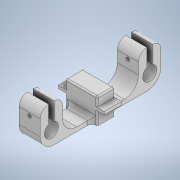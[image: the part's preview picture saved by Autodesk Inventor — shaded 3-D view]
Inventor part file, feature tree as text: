
AUTODESK INVENTOR PART (.ipt)
format: ipt  version: 2022 (Build 260153000, 153)  size: 273,920 bytes
history: native  units: mm
features: extrude x8, sketch x8, fillet x6
ambient origin geometry x8: Origin, YZ Plane, XZ Plane, XY Plane, X Axis, Y Axis, Z Axis, Center Point
bodies: Solido1 (feature_tree)
feature tree (22):
  extrude  "Estrusione1"  Depth=15.0mm
  extrude  "Estrusione2"  Depth=86.0mm
  extrude  "Estrusione3"  Depth=3.0mm TaperAngle=0.0deg
  fillet  "Raccordo1"  Radius=15.0mm
  fillet  "Raccordo2"  Radius=16.0mm
  extrude  "Estrusione4"  TaperAngle=0.0deg  [1 undecoded]
  extrude  "Estrusione5"  TaperAngle=0.0deg  [1 undecoded]
  fillet  "Raccordo3"  Radius=16.0mm
  extrude  "Estrusione6"  Depth=24.0mm TaperAngle=0.0deg
  extrude  "Estrusione7"  Depth=10.0mm
  extrude  "Estrusione8"  Depth=8.0mm
  fillet  "Raccordo4"  Radius=10.0mm
  fillet  "Raccordo5"  Radius=8.0mm
  fillet  "Raccordo6"  Radius=10.0mm
  sketch  "Schizzo1"
  sketch  "Schizzo2"
  sketch  "Schizzo3"
  sketch  "Schizzo4"
  sketch  "Schizzo5"
  sketch  "Schizzo6"
  sketch  "Schizzo7"
  sketch  "Schizzo8"
note: 2 required parameter values undecoded (feature->parameter linkage not recoverable at this tier; creation-order binding heuristic only, values carry confidence <= 0.55)
